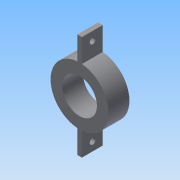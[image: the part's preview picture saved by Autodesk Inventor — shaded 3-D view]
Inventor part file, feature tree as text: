
AUTODESK INVENTOR PART (.ipt)
format: ipt  version: 2015 (Build 190159000, 159)  size: 106,496 bytes
history: native  units: mm
features: extrude x2, sketch x2
ambient origin geometry x8: Origin, YZ Plane, XZ Plane, XY Plane, X Axis, Y Axis, Z Axis, Center Point
bodies: Body1 (feature_tree)
feature tree (4):
  extrude  "Extrusion6"  Depth=40.0mm
  extrude  "Extrusion7"  Depth=18.0mm
  sketch  "Sketch4"  dims[d1=80.0mm d25=2.0mm d27=40.0mm]
  sketch  "Sketch5"  dims[d42=30.0mm d43=40.0mm d44=2.0mm d45=45.0mm d46=18.0mm d47=0.0mm d48=5.0mm d49=5.0mm d50=75.0mm d52=37.5mm d53=18.0mm d54=0.0mm]
